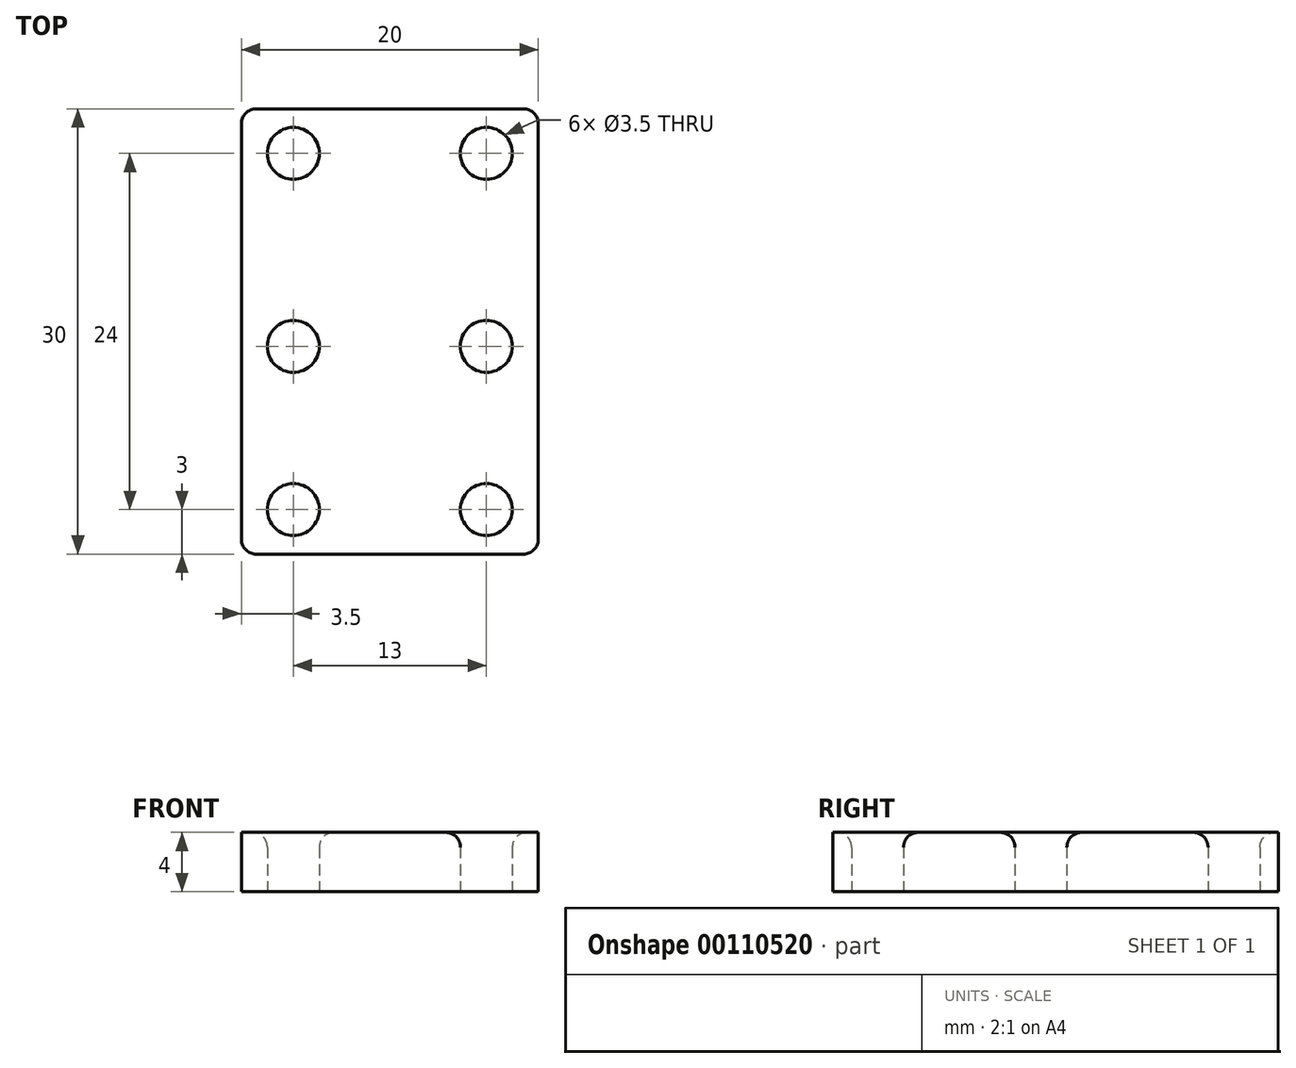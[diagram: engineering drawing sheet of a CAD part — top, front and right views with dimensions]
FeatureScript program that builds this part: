
annotation { "Feature Type Name" : "Feature", "Feature Type Description" : "" }
export const myFeature = defineFeature(function(context is Context, id is Id, definition is map)
    precondition{}
    {
        {
            var Q0;
            Q0=qCreatedBy(makeId("Top.planeOp"),FACE);
            var sketch = newSketch(context, id + "F0", { "sketchPlane" : qUnion([Q0])});
            skCircle(sketch, "E0", {"center": v(0, 0) * mm, "radius": 1.75 * mm});
            skCircle(sketch, "E1", {"center": v(13, 0) * mm, "radius": 1.75 * mm});
            skCircle(sketch, "E2", {"center": v(0, -13) * mm, "radius": 1.75 * mm});
            skCircle(sketch, "E3", {"center": v(13, -13) * mm, "radius": 1.75 * mm});
            skCircle(sketch, "E4", {"center": v(0, -24) * mm, "radius": 1.75 * mm});
            skCircle(sketch, "E5", {"center": v(13, -24) * mm, "radius": 1.75 * mm});
            skLineSegment(sketch, "E6.bottom", {"start": v(-3.5, 3) * mm, "end": v(16.5, 3) * mm});
            skLineSegment(sketch, "E6.top", {"start": v(-3.5, -27) * mm, "end": v(16.5, -27) * mm});
            skLineSegment(sketch, "E6.left", {"start": v(-3.5, 3) * mm, "end": v(-3.5, -27) * mm});
            skLineSegment(sketch, "E6.right", {"start": v(16.5, 3) * mm, "end": v(16.5, -27) * mm});
            skSolve(sketch);
        }
        {
            var Q0;
            Q0 = qSketchRegion(id + "F0", true);
            extrude(context, id + "F1", {"entities" : qUnion([Q0]), "depth" : 4 * mm});
        }
        {
            var Q0;
            Q0=makeQuery(id+"F1.opExtrude","CAP_EDGE",EDGE,{"disambiguationData":[OSD([sQuery(id+"F0.wireOp",EDGE,"E0")])],"isStart":false});
            var Q1;
            Q1=makeQuery(id+"F1.opExtrude","CAP_EDGE",EDGE,{"disambiguationData":[OSD([sQuery(id+"F0.wireOp",EDGE,"E1")])],"isStart":false});
            var Q2;
            Q2=makeQuery(id+"F1.opExtrude","CAP_EDGE",EDGE,{"disambiguationData":[OSD([sQuery(id+"F0.wireOp",EDGE,"E3")])],"isStart":false});
            var Q3;
            Q3=makeQuery(id+"F1.opExtrude","CAP_EDGE",EDGE,{"disambiguationData":[OSD([sQuery(id+"F0.wireOp",EDGE,"E2")])],"isStart":false});
            var Q4;
            Q4=makeQuery(id+"F1.opExtrude","CAP_EDGE",EDGE,{"disambiguationData":[OSD([sQuery(id+"F0.wireOp",EDGE,"E4")])],"isStart":false});
            var Q5;
            Q5=makeQuery(id+"F1.opExtrude","CAP_EDGE",EDGE,{"disambiguationData":[OSD([sQuery(id+"F0.wireOp",EDGE,"E5")])],"isStart":false});
            fillet(context, id + "F2", {"entities" : qUnion([Q0, Q1, Q2, Q3, Q4, Q5]), "radius" : 1 * mm, "tangentPropagation" : true, "allowEdgeOverflow" : false});
        }
        {
            var Q0;
            Q0=makeQuery(id+"F1.opExtrude","SWEPT_EDGE",EDGE,{"disambiguationData":[OSD([sQuery(id+"F0.wireOp",EDGE,"E6.bottom"),sQuery(id+"F0.wireOp",EDGE,"E6.left")])]});
            var Q1;
            Q1=makeQuery(id+"F1.opExtrude","SWEPT_EDGE",EDGE,{"disambiguationData":[OSD([sQuery(id+"F0.wireOp",EDGE,"E6.top"),sQuery(id+"F0.wireOp",EDGE,"E6.left")])]});
            var Q2;
            Q2=makeQuery(id+"F1.opExtrude","SWEPT_EDGE",EDGE,{"disambiguationData":[OSD([sQuery(id+"F0.wireOp",EDGE,"E6.top"),sQuery(id+"F0.wireOp",EDGE,"E6.right")])]});
            var Q3;
            Q3=makeQuery(id+"F1.opExtrude","SWEPT_EDGE",EDGE,{"disambiguationData":[OSD([sQuery(id+"F0.wireOp",EDGE,"E6.bottom"),sQuery(id+"F0.wireOp",EDGE,"E6.right")])]});
            fillet(context, id + "F3", {"entities" : qUnion([Q0, Q1, Q2, Q3]), "radius" : 1 * mm, "tangentPropagation" : true, "allowEdgeOverflow" : false});
        }
    });
